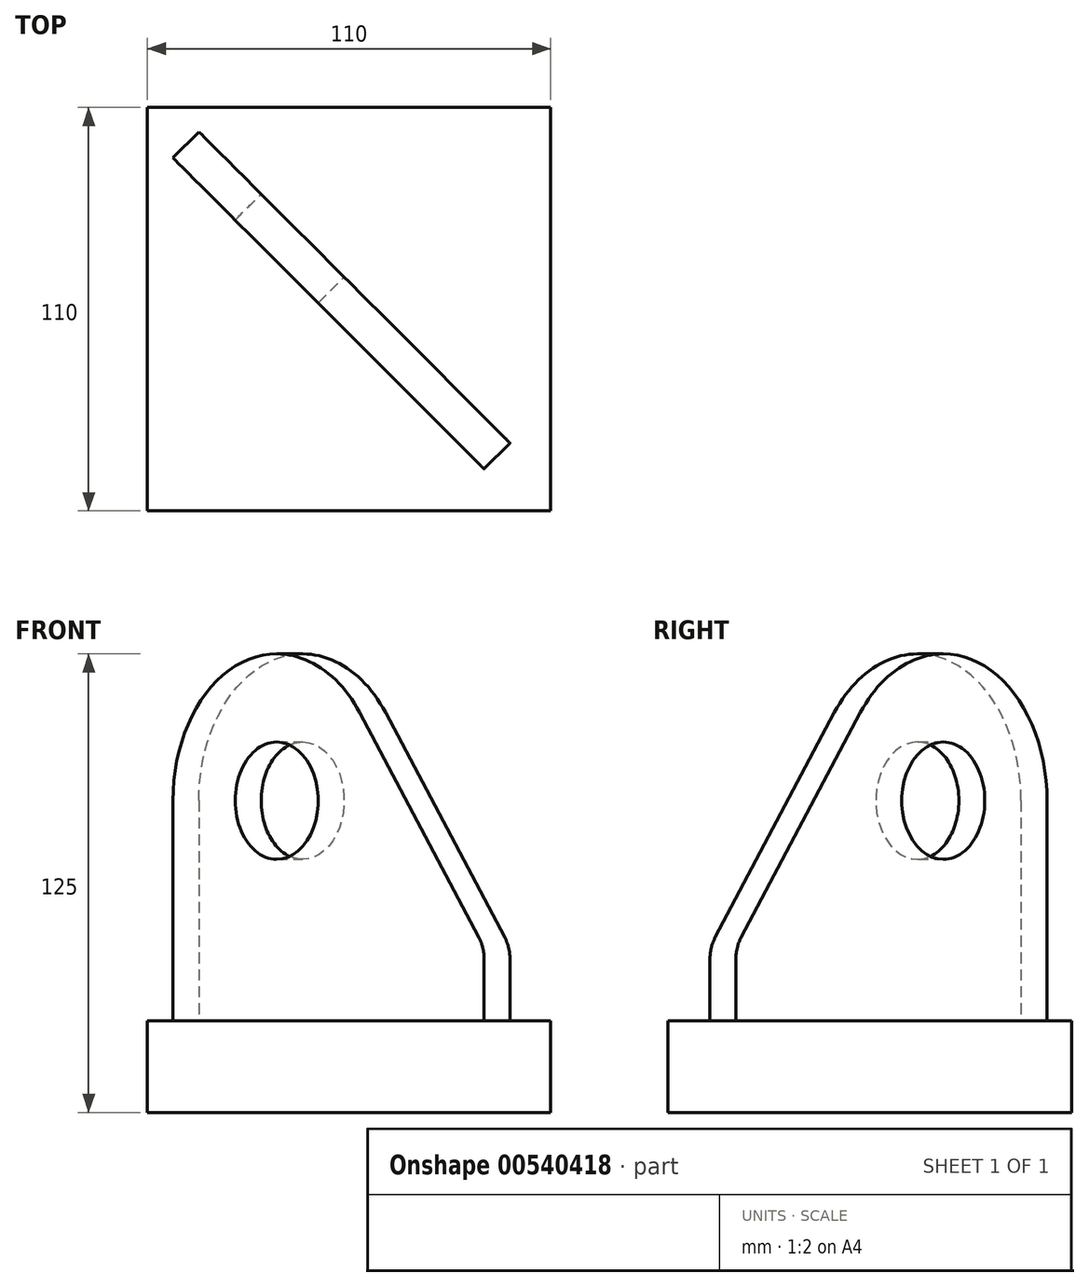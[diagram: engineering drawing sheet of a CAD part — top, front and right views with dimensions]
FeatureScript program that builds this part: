
annotation { "Feature Type Name" : "Feature", "Feature Type Description" : "" }
export const myFeature = defineFeature(function(context is Context, id is Id, definition is map)
    precondition{}
    {
        {
            var Q0;
            Q0=qCreatedBy(makeId("Top.planeOp"),FACE);
            var sketch = newSketch(context, id + "F0", { "sketchPlane" : qUnion([Q0])});
            skLineSegment(sketch, "E0.bottom", {"start": v(0, 0) * mm, "end": v(110, 0) * mm});
            skLineSegment(sketch, "E0.top", {"start": v(0, 110) * mm, "end": v(110, 110) * mm});
            skLineSegment(sketch, "E0.left", {"start": v(0, 0) * mm, "end": v(0, 110) * mm});
            skLineSegment(sketch, "E0.right", {"start": v(110, 0) * mm, "end": v(110, 110) * mm});
            skSolve(sketch);
        }
        {
            var Q0;
            Q0 = qSketchRegion(id + "F0", true);
            extrude(context, id + "F1", {"entities" : qUnion([Q0]), "depth" : 25 * mm, "offsetDistance" : 25 * mm});
        }
        {
            var Q0;
            Q0=makeQuery(id+"F1.opExtrude","CAP_FACE",FACE,{"disambiguationData":[OSD([sQuery(id+"F0.wireOp",EDGE,"E0.bottom"),sQuery(id+"F0.wireOp",EDGE,"E0.top"),sQuery(id+"F0.wireOp",EDGE,"E0.left"),sQuery(id+"F0.wireOp",EDGE,"E0.right")])],"isStart":false});
            var sketch = newSketch(context, id + "F2", { "sketchPlane" : qUnion([Q0])});
            skLineSegment(sketch, "E1", {"start": v(6.97, 96.26) * mm, "end": v(91.83, 11.41) * mm});
            skLineSegment(sketch, "E2", {"start": v(91.83, 11.41) * mm, "end": v(98.9, 18.48) * mm});
            skLineSegment(sketch, "E3", {"start": v(98.9, 18.48) * mm, "end": v(14.05, 103.33) * mm});
            skLineSegment(sketch, "E4", {"start": v(14.05, 103.33) * mm, "end": v(6.97, 96.26) * mm});
            skSolve(sketch);
        }
        {
            var Q0;
            Q0 = qSketchRegion(id + "F2", true);
            extrude(context, id + "F3", {"entities" : qUnion([Q0]), "operationType" : NewBodyOperationType.ADD, "depth" : 120 * mm, "offsetDistance" : 25 * mm});
        }
        {
            var Q0;
            Q0=makeQuery(id+"F3.opExtrude","SWEPT_FACE",FACE,{"disambiguationData":[OSD([sQuery(id+"F2.wireOp",EDGE,"E3")])]});
            var sketch = newSketch(context, id + "F4", { "sketchPlane" : qUnion([Q0])});
            skLineSegment(sketch, "E5", {"start": v(63.14, 85) * mm, "end": v(23.14, 85) * mm, "construction": true});
            skArc(sketch, "E6", {"start": v(63.14, 85) * mm, "mid": v(35.79, 122.95) * mm, "end": v(-8.86, 109) * mm});
            skCircle(sketch, "E7", {"center": v(23.14, 85) * mm, "radius": 16 * mm});
            skLineSegment(sketch, "E8", {"start": v(-54.86, 47.67) * mm, "end": v(-8.86, 109) * mm});
            skPoint(sketch, "E9.visualSharp", {"position": v(-56.86, 45) * mm});
            skArc(sketch, "E9.filletArc", {"start": v(-54.86, 47.67) * mm, "mid": v(-56.35, 44.83) * mm, "end": v(-56.86, 41.67) * mm});
            skLineSegment(sketch, "E10", {"start": v(-56.86, 41.67) * mm, "end": v(-56.86, 158.17) * mm});
            skLineSegment(sketch, "E11", {"start": v(-56.86, 158.17) * mm, "end": v(63.25, 158.17) * mm});
            skLineSegment(sketch, "E12", {"start": v(63.25, 158.17) * mm, "end": v(63.14, 85) * mm});
            skSolve(sketch);
        }
        {
            var Q0;
            Q0 = qSketchRegion(id + "F4", true);
            extrude(context, id + "F5", {"entities" : qUnion([Q0]), "operationType" : NewBodyOperationType.REMOVE, "oppositeDirection" : true, "depth" : 25 * mm, "offsetDistance" : 25 * mm});
        }
    });
